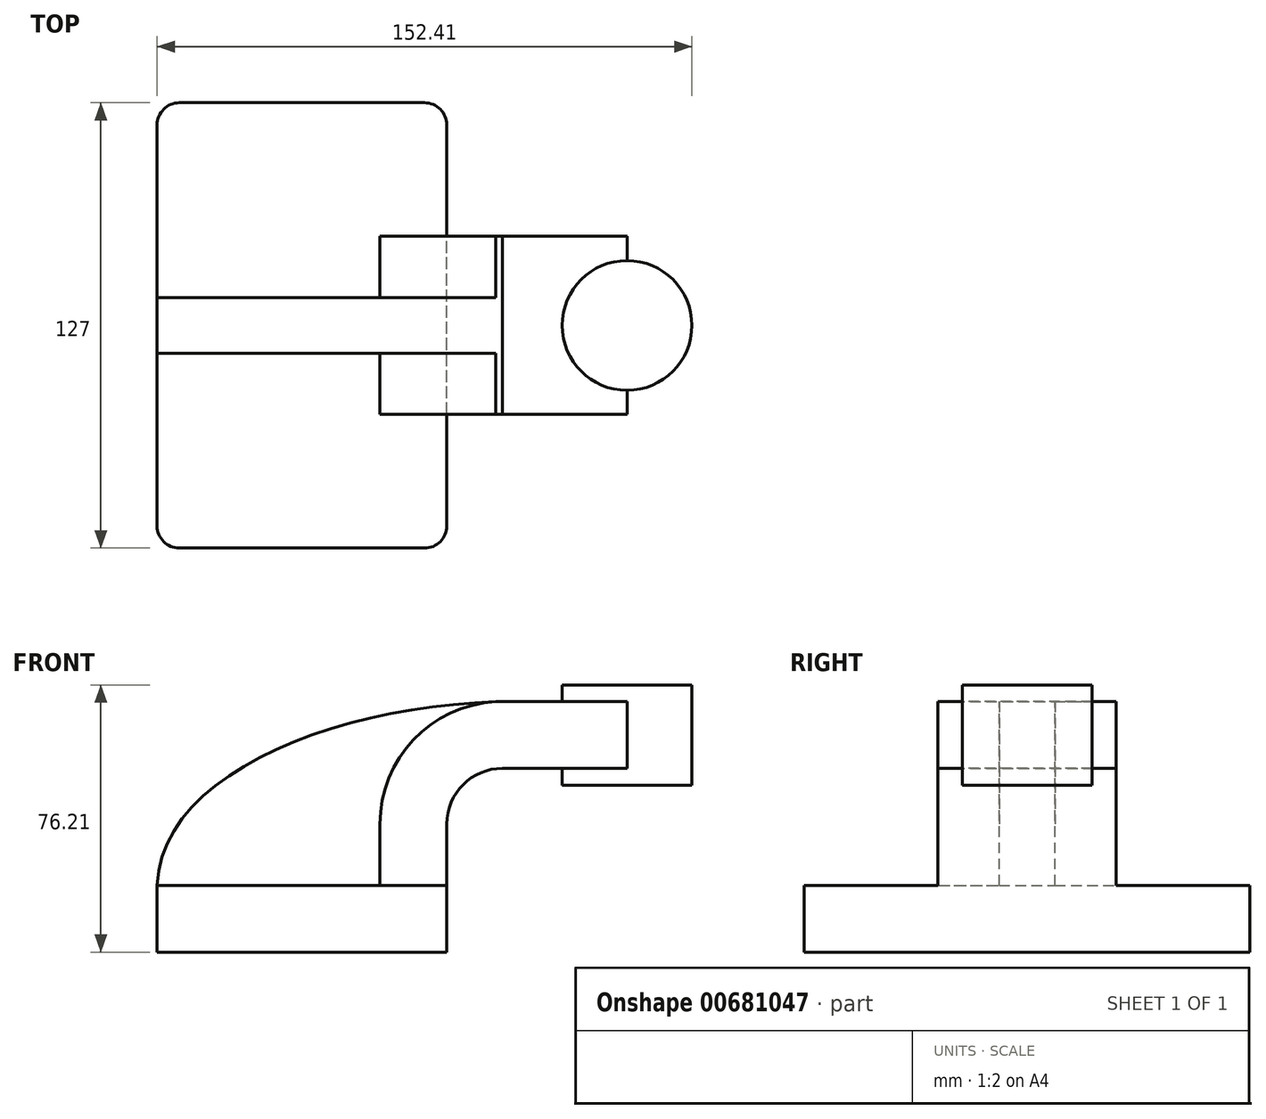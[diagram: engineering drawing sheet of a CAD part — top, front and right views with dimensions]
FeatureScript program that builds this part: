
annotation { "Feature Type Name" : "Feature", "Feature Type Description" : "" }
export const myFeature = defineFeature(function(context is Context, id is Id, definition is map)
    precondition{}
    {
        {
            var Q0;
            Q0=qCreatedBy(makeId("Front.planeOp"),FACE);
            var sketch = newSketch(context, id + "F0", { "sketchPlane" : qUnion([Q0])});
            skLineSegment(sketch, "E0.bottom", {"start": v(41.27, 9.53) * mm, "end": v(-41.28, 9.53) * mm});
            skLineSegment(sketch, "E0.top", {"start": v(41.28, -9.52) * mm, "end": v(-41.27, -9.52) * mm});
            skLineSegment(sketch, "E0.left", {"start": v(41.28, 9.53) * mm, "end": v(41.28, -9.52) * mm});
            skLineSegment(sketch, "E0.right", {"start": v(-41.28, 9.53) * mm, "end": v(-41.27, -9.52) * mm});
            skPoint(sketch, "E0.middle", {"position": v(0, 0) * mm});
            skLineSegment(sketch, "E1.bottom", {"start": v(111.12, 38.1) * mm, "end": v(60.33, 38.1) * mm});
            skLineSegment(sketch, "E1.top", {"start": v(111.13, 66.68) * mm, "end": v(60.33, 66.68) * mm});
            skLineSegment(sketch, "E1.left", {"start": v(111.12, 38.1) * mm, "end": v(111.12, 66.68) * mm});
            skLineSegment(sketch, "E1.right", {"start": v(60.33, 38.1) * mm, "end": v(60.33, 66.68) * mm});
            skPoint(sketch, "E1.middle", {"position": v(85.73, 52.39) * mm});
            skLineSegment(sketch, "E2", {"start": v(41.27, 9.53) * mm, "end": v(41.27, 27) * mm});
            skArc(sketch, "E3", {"start": v(41.27, 27) * mm, "mid": v(45.92, 38.23) * mm, "end": v(57.15, 42.88) * mm});
            skLineSegment(sketch, "E4", {"start": v(57.15, 42.88) * mm, "end": v(92.63, 42.88) * mm});
            skLineSegment(sketch, "E5.0", {"start": v(57.15, 61.93) * mm, "end": v(92.63, 61.93) * mm});
            skArc(sketch, "E5.1", {"start": v(22.23, 27) * mm, "mid": v(32.45, 51.7) * mm, "end": v(57.15, 61.93) * mm});
            skLineSegment(sketch, "E5.2", {"start": v(22.23, 9.53) * mm, "end": v(22.23, 27) * mm});
            skLineSegment(sketch, "E6", {"start": v(92.63, 66.68) * mm, "end": v(92.63, 38.1) * mm});
            skPoint(sketch, "E6.endSnap0", {"position": v(85.73, 38.1) * mm});
            skFitSpline(sketch, "E7", {"points": [v(-41.28, 9.53) * mm, v(57.15, 61.93) * mm], "startDerivative": vector(3.99, 97.27) * mm, "endDerivative": vector(139.46, 3.16) * mm});
            skSolve(sketch);
        }
        {
            var Q0;
            Q0=makeQuery(id+"F0.imprint","IMPRINT",FACE,{"disambiguationData":[TD([[makeQuery(id+"F0.imprint","IMPRINT",EDGE,{"derivedFrom":sQuery(id+"F0.wireOp",EDGE,"E0.top")}),-1.0]])]});
            extrude(context, id + "F1", {"entities" : qUnion([Q0]), "endBound" : BoundingType.SYMMETRIC, "depth" : 127 * mm, "offsetDistance" : 25.4 * mm});
        }
        {
            var Q0;
            {var subQ1=sQuery(id+"F0.wireOp",EDGE,"E2");Q0=makeQuery(id+"F0.imprint","IMPRINT",FACE,{"disambiguationData":[TD([[makeQuery(id+"F0.imprint","IMPRINT",EDGE,{"derivedFrom":subQ1}),1.0]])]});}
            var Q1;
            {var subQ0=sQuery(id+"F0.wireOp",EDGE,"E4");var subQ1=sQuery(id+"F0.wireOp",EDGE,"E1.right");var subQ2=makeQuery(id+"F0.imprint","INTERSECT",VERTEX,{"derivedFrom":[subQ1,subQ0]});Q1=makeQuery(id+"F0.imprint","IMPRINT",FACE,{"disambiguationData":[TD([[makeQuery(id+"F0.imprint","IMPRINT",EDGE,{"disambiguationData":[TD([[subQ2,-1.0]])],"derivedFrom":subQ1}),-1.0]])]});}
            extrude(context, id + "F2", {"entities" : qUnion([Q0, Q1]), "operationType" : NewBodyOperationType.ADD, "endBound" : BoundingType.SYMMETRIC, "depth" : 50.8 * mm, "offsetDistance" : 25.4 * mm});
        }
        {
            var Q0;
            {var subQ3=sQuery(id+"F0.wireOp",EDGE,"E5.2");Q0=makeQuery(id+"F0.imprint","IMPRINT",FACE,{"disambiguationData":[TD([[makeQuery(id+"F0.imprint","IMPRINT",EDGE,{"derivedFrom":subQ3}),1.0]])]});}
            extrude(context, id + "F3", {"entities" : qUnion([Q0]), "operationType" : NewBodyOperationType.ADD, "endBound" : BoundingType.SYMMETRIC, "depth" : 15.88 * mm, "offsetDistance" : 25.4 * mm});
        }
        {
            var Q0;
            {var subQ0=sQuery(id+"F0.wireOp",EDGE,"E1.left");Q0=makeQuery(id+"F0.imprint","IMPRINT",FACE,{"disambiguationData":[TD([[makeQuery(id+"F0.imprint","IMPRINT",EDGE,{"derivedFrom":subQ0}),1.0]])]});}
            var Q1;
            Q1=sQuery(id+"F0.wireOp",EDGE,"E6");
            revolve(context, id + "F4", {"operationType" : NewBodyOperationType.ADD, "entities" : qUnion([Q0]), "axis" : qUnion([Q1]), "revolveType" : RevolveType.FULL});
        }
        {
            var Q0;
            Q0=makeQuery(id+"F1.opExtrude","CAP_EDGE",EDGE,{"disambiguationData":[OSD([sQuery(id+"F0.wireOp",EDGE,"E0.left")])],"isStart":false});
            var Q1;
            Q1=makeQuery(id+"F1.opExtrude","CAP_EDGE",EDGE,{"disambiguationData":[OSD([sQuery(id+"F0.wireOp",EDGE,"E0.left")])],"isStart":true});
            var Q2;
            Q2=makeQuery(id+"F1.opExtrude","CAP_EDGE",EDGE,{"disambiguationData":[OSD([sQuery(id+"F0.wireOp",EDGE,"E0.right")])],"isStart":true});
            var Q3;
            Q3=makeQuery(id+"F1.opExtrude","CAP_EDGE",EDGE,{"disambiguationData":[OSD([sQuery(id+"F0.wireOp",EDGE,"E0.right")])],"isStart":false});
            fillet(context, id + "F5", {"entities" : qUnion([Q0, Q1, Q2, Q3]), "radius" : 6.35 * mm, "tangentPropagation" : true, "allowEdgeOverflow" : false});
        }
    });
